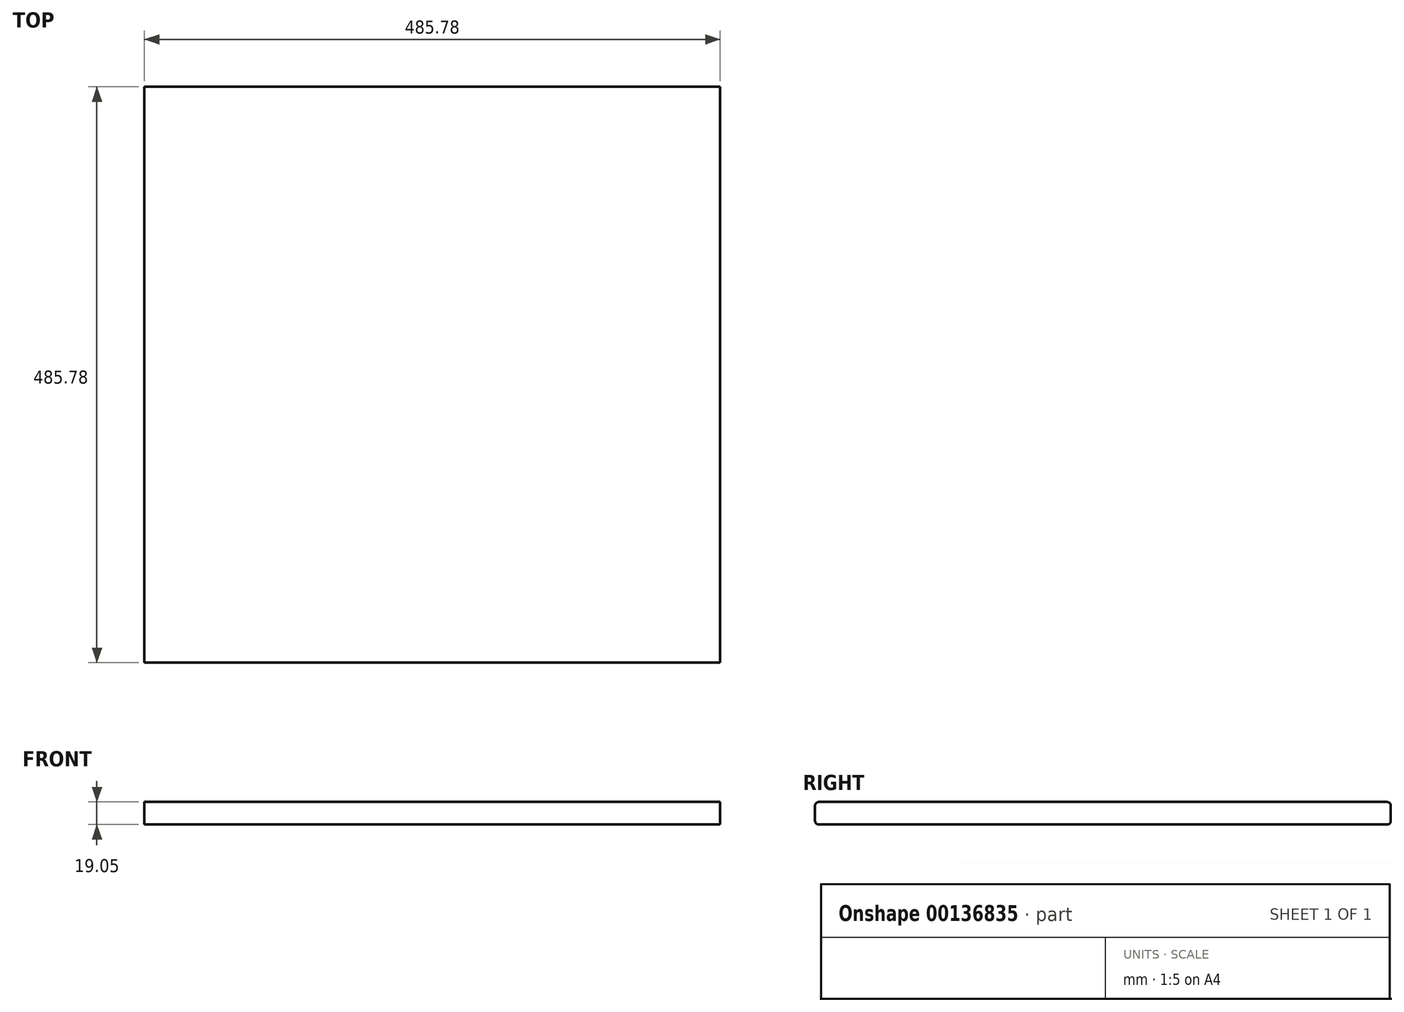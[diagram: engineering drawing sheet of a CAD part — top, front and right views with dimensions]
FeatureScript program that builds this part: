
annotation { "Feature Type Name" : "Feature", "Feature Type Description" : "" }
export const myFeature = defineFeature(function(context is Context, id is Id, definition is map)
    precondition{}
    {
        {
            var Q0;
            Q0=qCreatedBy(makeId("Top.planeOp"),FACE);
            var sketch = newSketch(context, id + "F0", { "sketchPlane" : qUnion([Q0])});
            skLineSegment(sketch, "E0.bottom", {"start": v(242.89, -242.89) * mm, "end": v(-242.89, -242.89) * mm});
            skLineSegment(sketch, "E0.top", {"start": v(242.89, 242.89) * mm, "end": v(-242.89, 242.89) * mm});
            skLineSegment(sketch, "E0.left", {"start": v(242.89, -242.89) * mm, "end": v(242.89, 242.89) * mm});
            skLineSegment(sketch, "E0.right", {"start": v(-242.89, -242.89) * mm, "end": v(-242.89, 242.89) * mm});
            skPoint(sketch, "E0.middle", {"position": v(0, 0) * mm});
            skSolve(sketch);
        }
        {
            var Q0;
            Q0=makeQuery(id+"F0.imprint","IMPRINT",FACE,{"disambiguationData":[TD([[makeQuery(id+"F0.imprint","IMPRINT",EDGE,{"derivedFrom":sQuery(id+"F0.wireOp",EDGE,"E0.bottom")}),-1.0]])]});
            extrude(context, id + "F1", {"entities" : qUnion([Q0]), "depth" : 19.05 * mm});
        }
        {
            var Q0;
            Q0=makeQuery(id+"F1.opExtrude","CAP_EDGE",EDGE,{"disambiguationData":[OSD([sQuery(id+"F0.wireOp",EDGE,"E0.bottom")])],"isStart":true});
            var Q1;
            Q1=makeQuery(id+"F1.opExtrude","CAP_EDGE",EDGE,{"disambiguationData":[OSD([sQuery(id+"F0.wireOp",EDGE,"E0.bottom")])],"isStart":false});
            var Q2;
            Q2=makeQuery(id+"F1.opExtrude","CAP_EDGE",EDGE,{"disambiguationData":[OSD([sQuery(id+"F0.wireOp",EDGE,"E0.top")])],"isStart":false});
            var Q3;
            Q3=makeQuery(id+"F1.opExtrude","CAP_EDGE",EDGE,{"disambiguationData":[OSD([sQuery(id+"F0.wireOp",EDGE,"E0.top")])],"isStart":true});
            fillet(context, id + "F2", {"entities" : qUnion([Q0, Q1, Q2, Q3]), "radius" : 3.17 * mm, "tangentPropagation" : true, "allowEdgeOverflow" : false});
        }
    });
